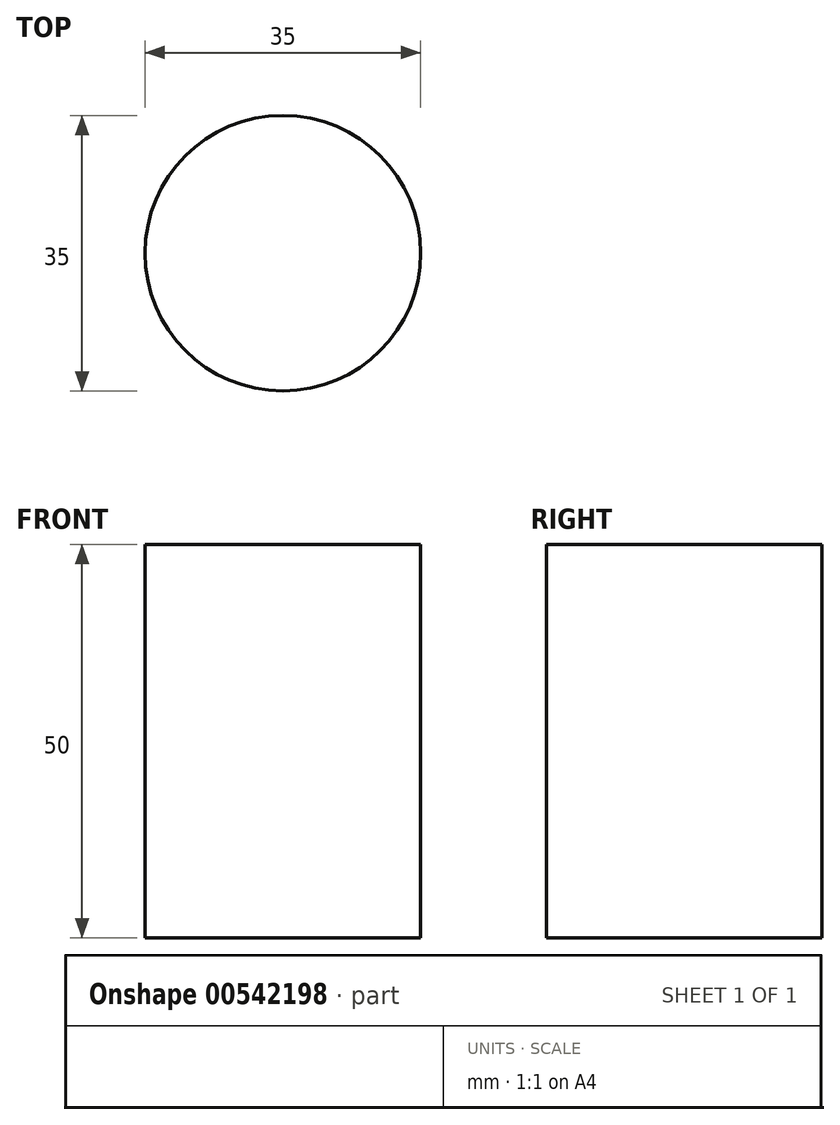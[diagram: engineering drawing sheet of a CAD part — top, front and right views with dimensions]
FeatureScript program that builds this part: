
annotation { "Feature Type Name" : "Feature", "Feature Type Description" : "" }
export const myFeature = defineFeature(function(context is Context, id is Id, definition is map)
    precondition{}
    {
        {
            var Q0;
            Q0=qCreatedBy(makeId("Top.planeOp"),FACE);
            var sketch = newSketch(context, id + "F0", { "sketchPlane" : qUnion([Q0])});
            skCircle(sketch, "E0", {"center": v(0, 0) * mm, "radius": 17.5 * mm});
            skSolve(sketch);
        }
        {
            var Q0;
            Q0=makeQuery(id+"F0.imprint","IMPRINT",FACE,{"disambiguationData":[TD([[makeQuery(id+"F0.imprint","IMPRINT",EDGE,{"derivedFrom":sQuery(id+"F0.wireOp",EDGE,"E0")}),1.0]])]});
            extrude(context, id + "F1", {"entities" : qUnion([Q0]), "depth" : 50 * mm, "offsetDistance" : 25 * mm});
        }
        {
            var Q0;
            Q0=qCreatedBy(makeId("Right.planeOp"),FACE);
            var sketch = newSketch(context, id + "F2", { "sketchPlane" : qUnion([Q0])});
            skFitSpline(sketch, "E1", {"points": [v(0, 5) * mm, v(-20, -11.55) * mm, v(-40, -50) * mm], "startDerivative": vector(-37.43, -32.07) * mm, "endDerivative": vector(-9.3, -86.42) * mm});
            skSolve(sketch);
        }
        {
            var Q0;
            Q0=qCreatedBy(makeId("Top.planeOp"),FACE);
            cPlane(context, id + "F3", {"entities" : qUnion([Q0]), "cplaneType" : CPlaneType.OFFSET, "offset" : 50 * mm, "oppositeDirection" : true, "width" : 150 * mm, "height" : 150 * mm});
        }
    });
